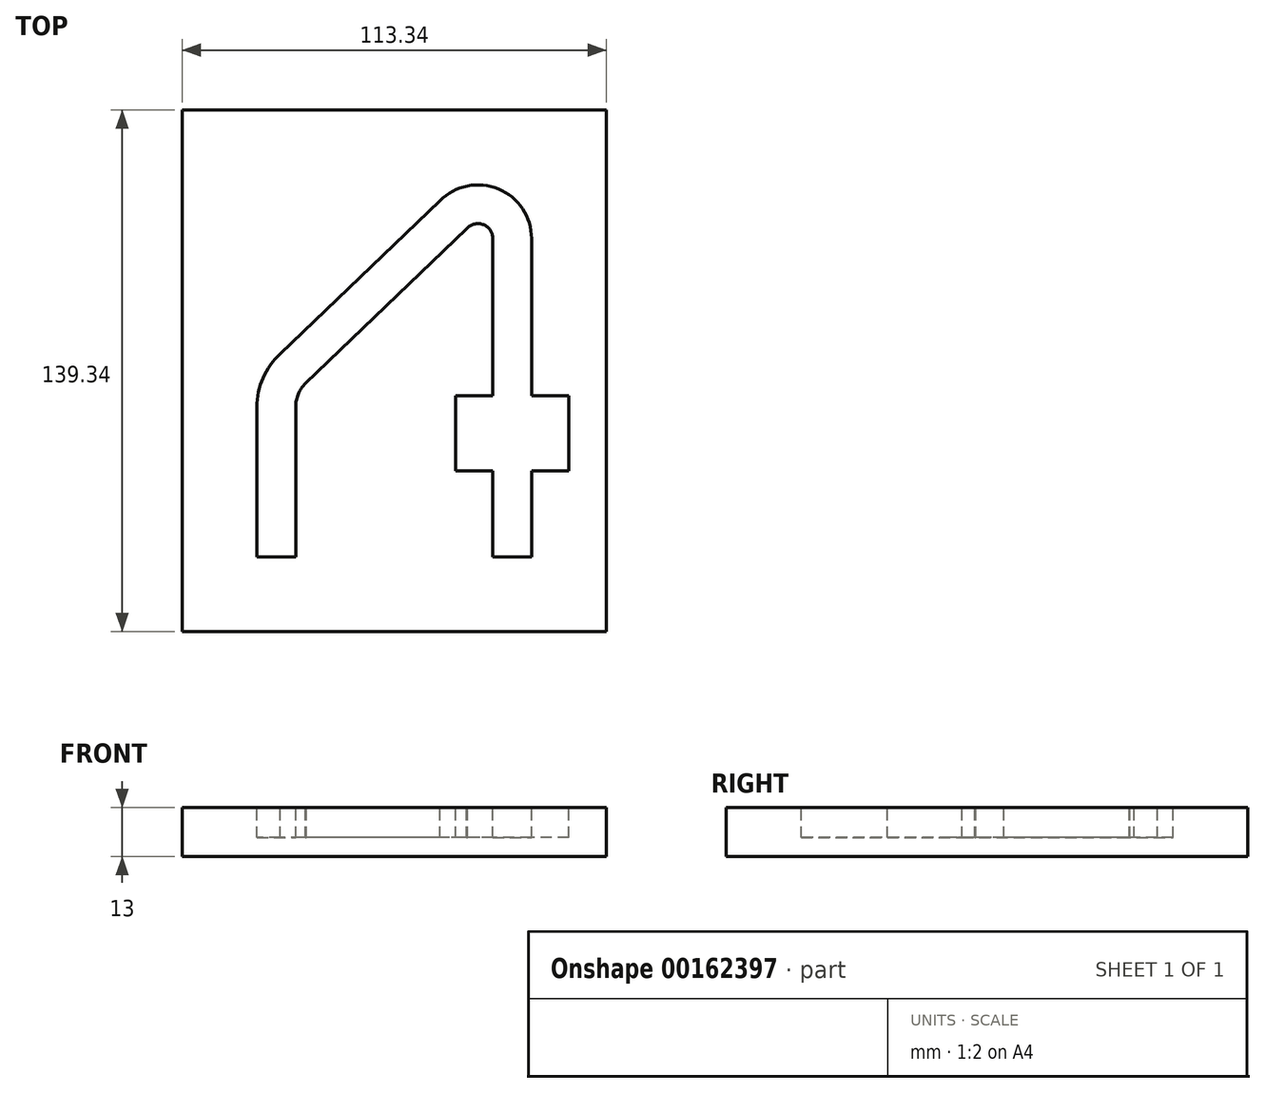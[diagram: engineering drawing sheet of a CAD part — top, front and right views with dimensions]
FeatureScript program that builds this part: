
annotation { "Feature Type Name" : "Feature", "Feature Type Description" : "" }
export const myFeature = defineFeature(function(context is Context, id is Id, definition is map)
    precondition{}
    {
        {
            var Q0;
            Q0=qCreatedBy(makeId("Top.planeOp"),FACE);
            var sketch = newSketch(context, id + "F0", { "sketchPlane" : qUnion([Q0])});
            skLineSegment(sketch, "E0", {"start": v(-56.67, -69.67) * mm, "end": v(-56.67, 69.67) * mm});
            skLineSegment(sketch, "E1", {"start": v(-56.67, -69.67) * mm, "end": v(56.67, -69.67) * mm});
            skLineSegment(sketch, "E2", {"start": v(56.67, -69.67) * mm, "end": v(56.67, 69.67) * mm});
            skLineSegment(sketch, "E3", {"start": v(-56.67, 69.67) * mm, "end": v(56.67, 69.67) * mm});
            skSolve(sketch);
        }
        {
            var Q0;
            Q0=makeQuery(id+"F0.imprint","IMPRINT",FACE,{"disambiguationData":[TD([[makeQuery(id+"F0.imprint","IMPRINT",EDGE,{"derivedFrom":sQuery(id+"F0.wireOp",EDGE,"E0")}),-1.0]])]});
            extrude(context, id + "F1", {"entities" : qUnion([Q0]), "depth" : 13 * mm});
        }
        {
            var Q0;
            Q0=makeQuery(id+"F1.opExtrude","CAP_FACE",FACE,{"disambiguationData":[OSD([sQuery(id+"F0.wireOp",EDGE,"E0"),sQuery(id+"F0.wireOp",EDGE,"E1"),sQuery(id+"F0.wireOp",EDGE,"E2"),sQuery(id+"F0.wireOp",EDGE,"E3")])],"isStart":false});
            var sketch = newSketch(context, id + "F2", { "sketchPlane" : qUnion([Q0])});
            skLineSegment(sketch, "E4", {"start": v(36.67, -49.67) * mm, "end": v(36.67, -26.67) * mm});
            skLineSegment(sketch, "E5", {"start": v(36.67, -6.67) * mm, "end": v(36.67, 35.33) * mm});
            skArc(sketch, "E6", {"start": v(12.2, 45.48) * mm, "mid": v(12.2, 45.47) * mm, "end": v(12.2, 45.47) * mm});
            skLineSegment(sketch, "E7", {"start": v(12.22, 45.48) * mm, "end": v(-30.99, 4.02) * mm});
            skLineSegment(sketch, "E8", {"start": v(-36.67, -49.67) * mm, "end": v(-36.67, -16.67) * mm});
            skLineSegment(sketch, "E9", {"start": v(-36.67, -9.67) * mm, "end": v(-36.67, -16.67) * mm});
            skLineSegment(sketch, "E10", {"start": v(-36.67, -49.67) * mm, "end": v(-26.33, -49.67) * mm});
            skLineSegment(sketch, "E11", {"start": v(-26.33, -49.67) * mm, "end": v(-26.33, -16.67) * mm});
            skLineSegment(sketch, "E12", {"start": v(26.33, -49.67) * mm, "end": v(26.33, -26.67) * mm});
            skLineSegment(sketch, "E13", {"start": v(-26.33, -9.67) * mm, "end": v(-26.33, -16.67) * mm});
            skArc(sketch, "E14", {"start": v(-23.7, -3.3) * mm, "mid": v(-23.7, -3.3) * mm, "end": v(-23.7, -3.3) * mm});
            skLineSegment(sketch, "E15", {"start": v(19.5, 38.15) * mm, "end": v(-23.71, -3.32) * mm});
            skLineSegment(sketch, "E16", {"start": v(26.33, -6.67) * mm, "end": v(26.33, 35.33) * mm});
            skLineSegment(sketch, "E17", {"start": v(26.33, -49.67) * mm, "end": v(36.67, -49.67) * mm});
            skLineSegment(sketch, "E18", {"start": v(46.67, -26.67) * mm, "end": v(46.67, -6.67) * mm});
            skLineSegment(sketch, "E19", {"start": v(16.33, -26.67) * mm, "end": v(16.33, -6.67) * mm});
            skLineSegment(sketch, "E20", {"start": v(46.67, -6.67) * mm, "end": v(36.67, -6.67) * mm});
            skLineSegment(sketch, "E21", {"start": v(46.67, -26.67) * mm, "end": v(36.67, -26.67) * mm});
            skLineSegment(sketch, "E22", {"start": v(26.33, -26.67) * mm, "end": v(16.33, -26.67) * mm});
            skLineSegment(sketch, "E23", {"start": v(26.33, -6.67) * mm, "end": v(16.33, -6.67) * mm});
            skLineSegment(sketch, "E24", {"start": v(-30.99, 4.02) * mm, "end": v(12.22, 45.48) * mm});
            skLineSegment(sketch, "E25", {"start": v(-23.7, -3.3) * mm, "end": v(19.5, 38.16) * mm});
            skLineSegment(sketch, "E26", {"start": v(-36.67, -16.67) * mm, "end": v(-36.67, -49.67) * mm});
            skLineSegment(sketch, "E27", {"start": v(-26.33, -16.67) * mm, "end": v(-26.33, -49.67) * mm});
            skLineSegment(sketch, "E28", {"start": v(-26.33, -49.67) * mm, "end": v(-36.67, -49.67) * mm});
            skLineSegment(sketch, "E29", {"start": v(26.33, 35.33) * mm, "end": v(26.33, -6.67) * mm});
            skLineSegment(sketch, "E30", {"start": v(36.67, 35.33) * mm, "end": v(36.67, -6.67) * mm});
            skLineSegment(sketch, "E31", {"start": v(16.33, -6.67) * mm, "end": v(16.33, -26.67) * mm});
            skLineSegment(sketch, "E32", {"start": v(16.33, -26.67) * mm, "end": v(26.33, -26.67) * mm});
            skLineSegment(sketch, "E33", {"start": v(26.33, -26.67) * mm, "end": v(26.33, -49.67) * mm});
            skLineSegment(sketch, "E34", {"start": v(36.67, -26.67) * mm, "end": v(46.67, -26.67) * mm});
            skArc(sketch, "E35", {"start": v(-11.4, 8.5) * mm, "mid": v(-11.4, 8.5) * mm, "end": v(-11.4, 8.5) * mm});
            skArc(sketch, "E36", {"start": v(9.67, 28.72) * mm, "mid": v(9.67, 28.72) * mm, "end": v(9.67, 28.72) * mm});
            skArc(sketch, "E37", {"start": v(19.33, 38) * mm, "mid": v(19.33, 38) * mm, "end": v(19.33, 38) * mm});
            skArc(sketch, "E38", {"start": v(9.64, 28.7) * mm, "mid": v(9.64, 28.7) * mm, "end": v(9.64, 28.7) * mm});
            skArc(sketch, "E39.trimOffspring", {"start": v(36.67, 35.33) * mm, "mid": v(27.82, 48.57) * mm, "end": v(12.2, 45.47) * mm});
            skArc(sketch, "E40", {"start": v(26.33, 35.33) * mm, "mid": v(23.87, 39.03) * mm, "end": v(19.5, 38.16) * mm});
            skArc(sketch, "E41", {"start": v(-23.42, -3.04) * mm, "mid": v(-25.57, -6.05) * mm, "end": v(-26.33, -9.67) * mm});
            skArc(sketch, "E42", {"start": v(-11.22, 8.67) * mm, "mid": v(-11.22, 8.67) * mm, "end": v(-11.22, 8.67) * mm});
            skArc(sketch, "E43.trimOffspring", {"start": v(-30.45, 4.54) * mm, "mid": v(-30.72, 4.28) * mm, "end": v(-30.99, 4.02) * mm});
            skArc(sketch, "E44.trimOffspring", {"start": v(-30.44, 4.55) * mm, "mid": v(-35.04, -1.9) * mm, "end": v(-36.67, -9.67) * mm});
            skSolve(sketch);
        }
        {
            var Q0;
            {var subQ4=sQuery(id+"F2.wireOp",EDGE,"E13");Q0=makeQuery(id+"F2.imprint","IMPRINT",FACE,{"disambiguationData":[TD([[makeQuery(id+"F2.imprint","IMPRINT",EDGE,{"derivedFrom":subQ4}),-1.0]])]});}
            var Q1;
            {var subQ0=sQuery(id+"F2.wireOp",EDGE,"E36");Q1=makeQuery(id+"F2.imprint","IMPRINT",FACE,{"disambiguationData":[TD([[makeQuery(id+"F2.imprint","IMPRINT",EDGE,{"derivedFrom":subQ0}),1.0]])]});}
            var Q2;
            {var subQ0=sQuery(id+"F2.wireOp",EDGE,"E38");Q2=makeQuery(id+"F2.imprint","IMPRINT",FACE,{"disambiguationData":[TD([[makeQuery(id+"F2.imprint","IMPRINT",EDGE,{"derivedFrom":subQ0}),-1.0]])]});}
            var Q3;
            {var subQ0=sQuery(id+"F2.wireOp",EDGE,"E35");Q3=makeQuery(id+"F2.imprint","IMPRINT",FACE,{"disambiguationData":[TD([[makeQuery(id+"F2.imprint","IMPRINT",EDGE,{"derivedFrom":subQ0}),1.0]])]});}
            var Q4;
            {var subQ0=sQuery(id+"F2.wireOp",EDGE,"E43.trimOffspring");Q4=makeQuery(id+"F2.imprint","IMPRINT",FACE,{"disambiguationData":[TD([[makeQuery(id+"F2.imprint","IMPRINT",EDGE,{"derivedFrom":subQ0}),1.0]])]});}
            var Q5;
            {var subQ0=sQuery(id+"F2.wireOp",EDGE,"E35");Q5=makeQuery(id+"F2.imprint","IMPRINT",FACE,{"disambiguationData":[TD([[makeQuery(id+"F2.imprint","IMPRINT",EDGE,{"derivedFrom":subQ0}),-1.0]])]});}
            var Q6;
            {var subQ0=sQuery(id+"F2.wireOp",EDGE,"E42");Q6=makeQuery(id+"F2.imprint","IMPRINT",FACE,{"disambiguationData":[TD([[makeQuery(id+"F2.imprint","IMPRINT",EDGE,{"derivedFrom":subQ0}),-1.0]])]});}
            var Q7;
            {var subQ0=sQuery(id+"F2.wireOp",EDGE,"E41");var subQ1=sQuery(id+"F2.wireOp",EDGE,"E25");var subQ2=makeQuery(id+"F2.imprint","INTERSECT",VERTEX,{"disambiguationData":[OD(0.0)],"derivedFrom":[subQ1,subQ0]});Q7=makeQuery(id+"F2.imprint","IMPRINT",FACE,{"disambiguationData":[TD([[makeQuery(id+"F2.imprint","IMPRINT",EDGE,{"disambiguationData":[TD([[subQ2,-1.0]])],"derivedFrom":subQ1}),1.0]])]});}
            var Q8;
            {var subQ0=sQuery(id+"F2.wireOp",EDGE,"E41");var subQ1=sQuery(id+"F2.wireOp",EDGE,"E15");var subQ2=makeQuery(id+"F2.imprint","INTERSECT",VERTEX,{"disambiguationData":[OD(0.0)],"derivedFrom":[subQ1,subQ0]});Q8=makeQuery(id+"F2.imprint","IMPRINT",FACE,{"disambiguationData":[TD([[makeQuery(id+"F2.imprint","IMPRINT",EDGE,{"disambiguationData":[TD([[subQ2,-1.0]])],"derivedFrom":subQ1}),-1.0]])]});}
            var Q9;
            {var subQ0=sQuery(id+"F2.wireOp",EDGE,"E36");Q9=makeQuery(id+"F2.imprint","IMPRINT",FACE,{"disambiguationData":[TD([[makeQuery(id+"F2.imprint","IMPRINT",EDGE,{"derivedFrom":subQ0}),-1.0]])]});}
            extrude(context, id + "F3", {"entities" : qUnion([Q0, Q1, Q2, Q3, Q4, Q5, Q6, Q7, Q8, Q9]), "operationType" : NewBodyOperationType.REMOVE, "oppositeDirection" : true, "depth" : 8 * mm});
        }
    });
